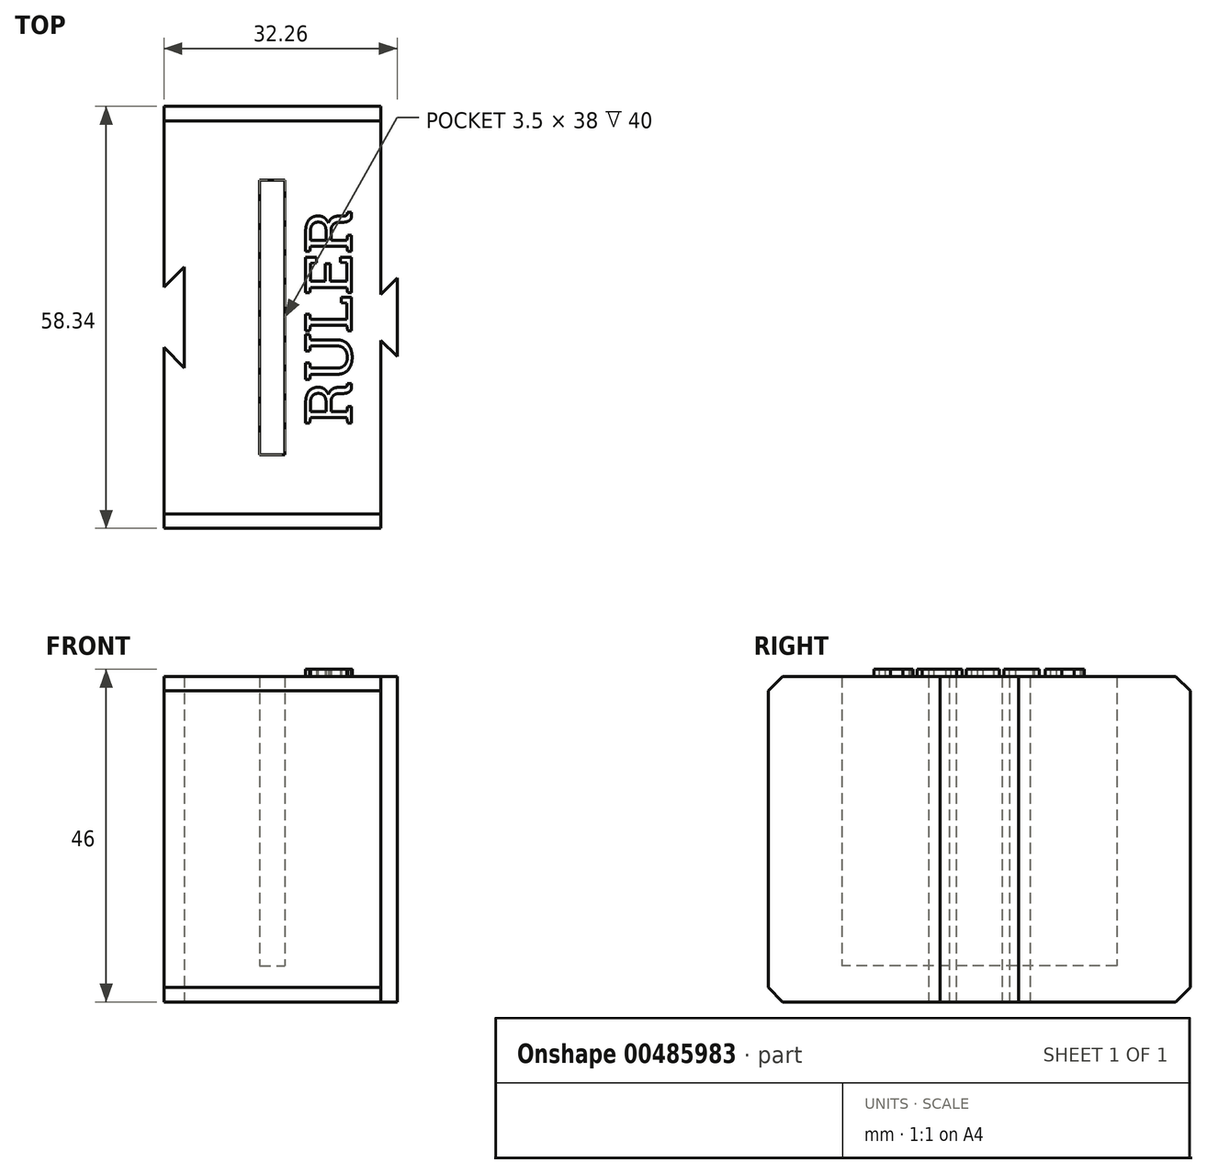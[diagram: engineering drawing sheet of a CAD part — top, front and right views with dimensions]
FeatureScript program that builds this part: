
annotation { "Feature Type Name" : "Feature", "Feature Type Description" : "" }
export const myFeature = defineFeature(function(context is Context, id is Id, definition is map)
    precondition{}
    {
        {
            var Q0;
            Q0=qCreatedBy(makeId("Top.planeOp"),FACE);
            var sketch = newSketch(context, id + "F0", { "sketchPlane" : qUnion([Q0])});
            skLineSegment(sketch, "E0", {"start": v(-15, 4.17) * mm, "end": v(-15, 29.17) * mm});
            skLineSegment(sketch, "E1", {"start": v(-15, 29.17) * mm, "end": v(15, 29.17) * mm});
            skLineSegment(sketch, "E2", {"start": v(15, 29.17) * mm, "end": v(15, 3.17) * mm});
            skLineSegment(sketch, "E3", {"start": v(-15, 4.17) * mm, "end": v(-12.17, 7) * mm});
            skLineSegment(sketch, "E4", {"start": v(-12.17, 7) * mm, "end": v(-12.17, 0) * mm});
            skLineSegment(sketch, "E5", {"start": v(15, 3.17) * mm, "end": v(17.26, 5.43) * mm});
            skLineSegment(sketch, "E6", {"start": v(17.26, 5.43) * mm, "end": v(17.26, -0.57) * mm});
            skLineSegment(sketch, "E7.MirrorCS", {"start": v(-15, -4.17) * mm, "end": v(-12.17, -7) * mm});
            skLineSegment(sketch, "E8.MirrorCS", {"start": v(15, -29.17) * mm, "end": v(15, -3.17) * mm});
            skLineSegment(sketch, "E9.MirrorCS", {"start": v(-12.17, -7) * mm, "end": v(-12.17, 0) * mm});
            skLineSegment(sketch, "E10.MirrorCS", {"start": v(-15, -4.17) * mm, "end": v(-15, -29.17) * mm});
            skLineSegment(sketch, "E11.MirrorCS", {"start": v(17.26, -5.43) * mm, "end": v(17.26, 0.57) * mm});
            skLineSegment(sketch, "E12.MirrorCS", {"start": v(15, -3.17) * mm, "end": v(17.26, -5.43) * mm});
            skLineSegment(sketch, "E13.MirrorCS", {"start": v(-15, -29.17) * mm, "end": v(15, -29.17) * mm});
            skLineSegment(sketch, "E14.bottom", {"start": v(-1.75, 19) * mm, "end": v(1.75, 19) * mm});
            skLineSegment(sketch, "E14.top", {"start": v(-1.75, -19) * mm, "end": v(1.75, -19) * mm});
            skLineSegment(sketch, "E14.left", {"start": v(-1.75, 19) * mm, "end": v(-1.75, -19) * mm});
            skLineSegment(sketch, "E14.right", {"start": v(1.75, 19) * mm, "end": v(1.75, -19) * mm});
            skPoint(sketch, "E14.middle", {"position": v(0, 0) * mm});
            skSolve(sketch);
        }
        {
            var Q0;
            Q0=qSketchRegion(id+"F0",true);
            extrude(context, id + "F1", {"entities" : qUnion([Q0]), "depth" : 40 * mm});
        }
        {
            var Q0;
            Q0=makeQuery(id+"F0.imprint","IMPRINT",FACE,{"disambiguationData":[TD([[makeQuery(id+"F0.imprint","IMPRINT",EDGE,{"derivedFrom":sQuery(id+"F0.wireOp",EDGE,"E0")}),-1.0]])]});
            var Q1;
            Q1=makeQuery(id+"F0.imprint","IMPRINT",FACE,{"disambiguationData":[TD([[makeQuery(id+"F0.imprint","IMPRINT",EDGE,{"derivedFrom":sQuery(id+"F0.wireOp",EDGE,"E14.bottom")}),-1.0]])]});
            extrude(context, id + "F2", {"entities" : qUnion([Q0, Q1]), "operationType" : NewBodyOperationType.ADD, "oppositeDirection" : true, "depth" : 5 * mm});
        }
        {
            var Q0;
            Q0=makeQuery(id+"F2.opExtrude","CAP_EDGE",EDGE,{"disambiguationData":[OSD([sQuery(id+"F0.wireOp",EDGE,"E13.MirrorCS")])],"isStart":false});
            var Q1;
            Q1=makeQuery(id+"F2.opExtrude","CAP_EDGE",EDGE,{"disambiguationData":[OSD([sQuery(id+"F0.wireOp",EDGE,"E1")])],"isStart":false});
            var Q2;
            Q2=makeQuery(id+"F1.opExtrude","CAP_EDGE",EDGE,{"disambiguationData":[OSD([sQuery(id+"F0.wireOp",EDGE,"E13.MirrorCS")])],"isStart":false});
            var Q3;
            Q3=makeQuery(id+"F1.opExtrude","CAP_EDGE",EDGE,{"disambiguationData":[OSD([sQuery(id+"F0.wireOp",EDGE,"E1")])],"isStart":false});
            chamfer(context, id + "F3", {"entities" : qUnion([Q0, Q1, Q2, Q3]), "width" : 2 * mm, "tangentPropagation" : true});
        }
        {
            var Q0;
            Q0=makeQuery(id+"F1.opExtrude","CAP_FACE",FACE,{"disambiguationData":[OSD([sQuery(id+"F0.wireOp",EDGE,"E0"),sQuery(id+"F0.wireOp",EDGE,"E1"),sQuery(id+"F0.wireOp",EDGE,"E2"),sQuery(id+"F0.wireOp",EDGE,"E3"),sQuery(id+"F0.wireOp",EDGE,"E4"),sQuery(id+"F0.wireOp",EDGE,"E5"),sQuery(id+"F0.wireOp",EDGE,"E6"),sQuery(id+"F0.wireOp",EDGE,"E7.MirrorCS"),sQuery(id+"F0.wireOp",EDGE,"E8.MirrorCS"),sQuery(id+"F0.wireOp",EDGE,"E9.MirrorCS"),sQuery(id+"F0.wireOp",EDGE,"E10.MirrorCS"),sQuery(id+"F0.wireOp",EDGE,"E11.MirrorCS"),sQuery(id+"F0.wireOp",EDGE,"E12.MirrorCS"),sQuery(id+"F0.wireOp",EDGE,"E13.MirrorCS"),sQuery(id+"F0.wireOp",EDGE,"E14.bottom"),sQuery(id+"F0.wireOp",EDGE,"E14.top"),sQuery(id+"F0.wireOp",EDGE,"E14.left"),sQuery(id+"F0.wireOp",EDGE,"E14.right")])],"isStart":false});
            var sketch = newSketch(context, id + "F4", { "sketchPlane" : qUnion([Q0])});
            skText(sketch, "E15", { "text": "RULER", "fontName": "RobotoSlab-Regular.ttf"});
            const initialGuessF4  = {"E15": [0.01094, -0.0149, 0, 1, 0.00643]};
            skSetInitialGuess(sketch, initialGuessF4);
            skSolve(sketch);
        }
        {
            var Q0;
            Q0=qSketchRegion(id+"F4",true);
            extrude(context, id + "F5", {"entities" : qUnion([Q0]), "operationType" : NewBodyOperationType.ADD, "depth" : 1 * mm});
        }
    });
